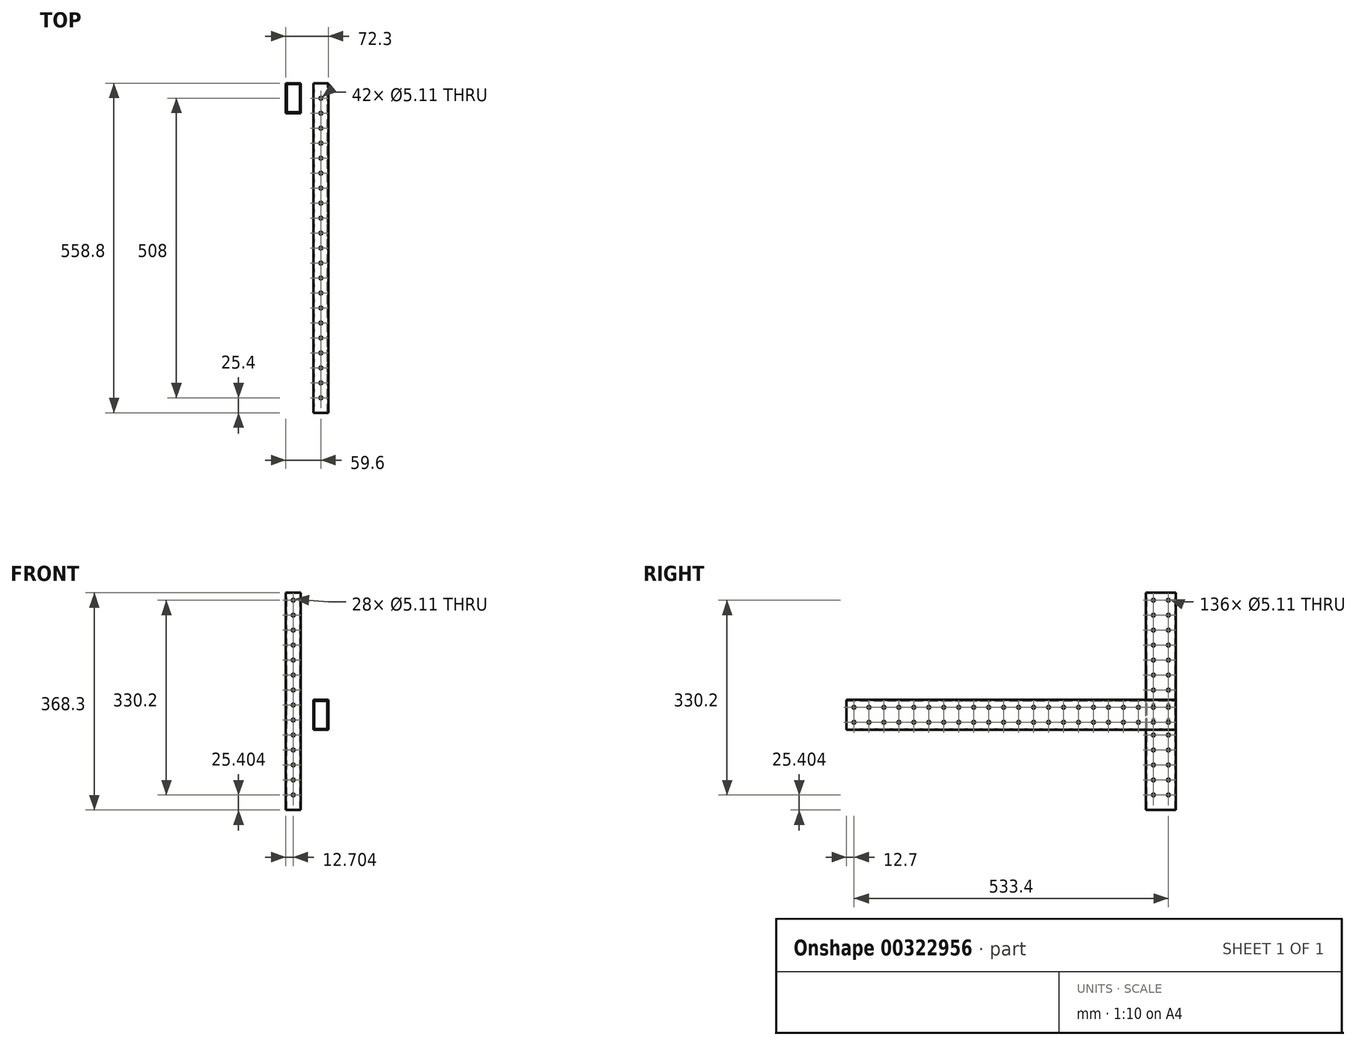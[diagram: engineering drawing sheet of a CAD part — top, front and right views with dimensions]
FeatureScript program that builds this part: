
annotation { "Feature Type Name" : "Feature", "Feature Type Description" : "" }
export const myFeature = defineFeature(function(context is Context, id is Id, definition is map)
    precondition{}
    {
        {
            var Q0;
            Q0=qCreatedBy(makeId("Front.planeOp"),FACE);
            var sketch = newSketch(context, id + "F0", { "sketchPlane" : qUnion([Q0])});
            skLineSegment(sketch, "E0.bottom", {"start": v(-59.6, -161.33) * mm, "end": v(-34.2, -161.33) * mm});
            skLineSegment(sketch, "E0.top", {"start": v(-59.6, 206.97) * mm, "end": v(-34.2, 206.97) * mm});
            skLineSegment(sketch, "E0.left", {"start": v(-59.6, -161.33) * mm, "end": v(-59.6, 206.97) * mm});
            skLineSegment(sketch, "E0.right", {"start": v(-34.2, -161.33) * mm, "end": v(-34.2, 206.97) * mm});
            skSolve(sketch);
        }
        {
            var Q0;
            Q0=makeQuery(id+"F0.imprint","IMPRINT",FACE,{"disambiguationData":[TD([[makeQuery(id+"F0.imprint","IMPRINT",EDGE,{"derivedFrom":sQuery(id+"F0.wireOp",EDGE,"E0.bottom")}),1.0]])]});
            extrude(context, id + "F1", {"entities" : qUnion([Q0]), "depth" : 50.8 * mm});
        }
        {
            var Q0;
            Q0=qCreatedBy(makeId("Front.planeOp"),FACE);
            var sketch = newSketch(context, id + "F2", { "sketchPlane" : qUnion([Q0])});
            skLineSegment(sketch, "E1.bottom", {"start": v(12.7, -25.4) * mm, "end": v(-12.7, -25.4) * mm});
            skLineSegment(sketch, "E1.top", {"start": v(12.7, 25.4) * mm, "end": v(-12.7, 25.4) * mm});
            skLineSegment(sketch, "E1.left", {"start": v(12.7, -25.4) * mm, "end": v(12.7, 25.4) * mm});
            skLineSegment(sketch, "E1.right", {"start": v(-12.7, -25.4) * mm, "end": v(-12.7, 25.4) * mm});
            skPoint(sketch, "E1.middle", {"position": v(0, 0) * mm});
            skLineSegment(sketch, "E2.bottom", {"start": v(11.11, -23.81) * mm, "end": v(-11.11, -23.81) * mm});
            skLineSegment(sketch, "E2.top", {"start": v(11.11, 23.81) * mm, "end": v(-11.11, 23.81) * mm});
            skLineSegment(sketch, "E2.left", {"start": v(11.11, -23.81) * mm, "end": v(11.11, 23.81) * mm});
            skLineSegment(sketch, "E2.right", {"start": v(-11.11, -23.81) * mm, "end": v(-11.11, 23.81) * mm});
            skSolve(sketch);
        }
        {
            var Q0;
            Q0=makeQuery(id+"F2.imprint","IMPRINT",FACE,{"disambiguationData":[TD([[makeQuery(id+"F2.imprint","IMPRINT",EDGE,{"derivedFrom":sQuery(id+"F2.wireOp",EDGE,"E1.bottom")}),-1.0]])]});
            extrude(context, id + "F3", {"entities" : qUnion([Q0]), "depth" : 558.8 * mm});
        }
        {
            var Q0;
            Q0=makeQuery(id+"F3.opExtrude","SWEPT_FACE",FACE,{"disambiguationData":[OSD([sQuery(id+"F2.wireOp",EDGE,"E1.top")])]});
            var sketch = newSketch(context, id + "F4", { "sketchPlane" : qUnion([Q0])});
            skCircle(sketch, "E3", {"center": v(0, -533.4) * mm, "radius": 2.55 * mm});
            skCircle(sketch, "E4.1.0.0", {"center": v(0, -508) * mm, "radius": 2.55 * mm});
            skCircle(sketch, "E4.2.0.0", {"center": v(0, -482.6) * mm, "radius": 2.55 * mm});
            skCircle(sketch, "E4.3.0.0", {"center": v(0, -457.2) * mm, "radius": 2.55 * mm});
            skCircle(sketch, "E4.4.0.0", {"center": v(0, -431.8) * mm, "radius": 2.55 * mm});
            skCircle(sketch, "E4.5.0.0", {"center": v(0, -406.4) * mm, "radius": 2.55 * mm});
            skCircle(sketch, "E4.6.0.0", {"center": v(0, -381) * mm, "radius": 2.55 * mm});
            skCircle(sketch, "E4.7.0.0", {"center": v(0, -355.6) * mm, "radius": 2.55 * mm});
            skCircle(sketch, "E4.8.0.0", {"center": v(0, -330.2) * mm, "radius": 2.55 * mm});
            skCircle(sketch, "E4.9.0.0", {"center": v(0, -304.8) * mm, "radius": 2.55 * mm});
            skCircle(sketch, "E4.10.0.0", {"center": v(0, -279.4) * mm, "radius": 2.55 * mm});
            skCircle(sketch, "E4.11.0.0", {"center": v(0, -254) * mm, "radius": 2.55 * mm});
            skCircle(sketch, "E4.12.0.0", {"center": v(0, -228.6) * mm, "radius": 2.55 * mm});
            skCircle(sketch, "E4.13.0.0", {"center": v(0, -203.2) * mm, "radius": 2.55 * mm});
            skCircle(sketch, "E4.14.0.0", {"center": v(0, -177.8) * mm, "radius": 2.55 * mm});
            skCircle(sketch, "E4.15.0.0", {"center": v(0, -152.4) * mm, "radius": 2.55 * mm});
            skCircle(sketch, "E4.16.0.0", {"center": v(0, -127) * mm, "radius": 2.55 * mm});
            skCircle(sketch, "E4.17.0.0", {"center": v(0, -101.6) * mm, "radius": 2.55 * mm});
            skCircle(sketch, "E4.18.0.0", {"center": v(0, -76.2) * mm, "radius": 2.55 * mm});
            skCircle(sketch, "E4.19.0.0", {"center": v(0, -50.8) * mm, "radius": 2.55 * mm});
            skCircle(sketch, "E4.20.0.0", {"center": v(0, -25.4) * mm, "radius": 2.55 * mm});
            skLineSegment(sketch, "E4.direction1", {"start": v(0, -533.4) * mm, "end": v(0, -508) * mm, "construction": true});
            skSolve(sketch);
        }
        {
            var Q0;
            Q0=makeQuery(id+"F1.opExtrude","CAP_FACE",FACE,{"disambiguationData":[OSD([sQuery(id+"F0.wireOp",EDGE,"E0.bottom"),sQuery(id+"F0.wireOp",EDGE,"E0.top"),sQuery(id+"F0.wireOp",EDGE,"E0.left"),sQuery(id+"F0.wireOp",EDGE,"E0.right")])],"isStart":false});
            var sketch = newSketch(context, id + "F5", { "sketchPlane" : qUnion([Q0])});
            skCircle(sketch, "E5", {"center": v(-46.9, 194.27) * mm, "radius": 2.55 * mm});
            skCircle(sketch, "E6.0.1.0", {"center": v(-46.9, 168.87) * mm, "radius": 2.55 * mm});
            skCircle(sketch, "E6.0.2.0", {"center": v(-46.9, 143.47) * mm, "radius": 2.55 * mm});
            skCircle(sketch, "E6.0.3.0", {"center": v(-46.9, 118.07) * mm, "radius": 2.55 * mm});
            skCircle(sketch, "E6.0.4.0", {"center": v(-46.9, 92.67) * mm, "radius": 2.55 * mm});
            skCircle(sketch, "E6.0.5.0", {"center": v(-46.9, 67.27) * mm, "radius": 2.55 * mm});
            skCircle(sketch, "E6.0.6.0", {"center": v(-46.9, 41.87) * mm, "radius": 2.55 * mm});
            skCircle(sketch, "E6.0.7.0", {"center": v(-46.9, 16.47) * mm, "radius": 2.55 * mm});
            skCircle(sketch, "E6.0.8.0", {"center": v(-46.9, -8.93) * mm, "radius": 2.55 * mm});
            skCircle(sketch, "E6.0.9.0", {"center": v(-46.9, -34.33) * mm, "radius": 2.55 * mm});
            skCircle(sketch, "E6.0.10.0", {"center": v(-46.9, -59.73) * mm, "radius": 2.55 * mm});
            skCircle(sketch, "E6.0.11.0", {"center": v(-46.9, -85.13) * mm, "radius": 2.55 * mm});
            skCircle(sketch, "E6.0.12.0", {"center": v(-46.9, -110.53) * mm, "radius": 2.55 * mm});
            skCircle(sketch, "E6.0.13.0", {"center": v(-46.9, -135.93) * mm, "radius": 2.55 * mm});
            skLineSegment(sketch, "E6.direction1", {"start": v(-46.9, 194.27) * mm, "end": v(-21.5, 194.27) * mm, "construction": true});
            skLineSegment(sketch, "E6.direction2", {"start": v(-46.9, 194.27) * mm, "end": v(-46.9, 168.87) * mm, "construction": true});
            skSolve(sketch);
        }
        {
            var Q0;
            Q0=sQuery(id+"F4.wireOp",VERTEX,"E3.center");
            var Q1;
            Q1=sQuery(id+"F4.wireOp",VERTEX,"E4.1.0.0.center");
            var Q2;
            Q2=sQuery(id+"F4.wireOp",VERTEX,"E4.2.0.0.center");
            var Q3;
            Q3=sQuery(id+"F4.wireOp",VERTEX,"E4.3.0.0.center");
            var Q4;
            Q4=sQuery(id+"F4.wireOp",VERTEX,"E4.4.0.0.center");
            var Q5;
            Q5=sQuery(id+"F4.wireOp",VERTEX,"E4.5.0.0.center");
            var Q6;
            Q6=sQuery(id+"F4.wireOp",VERTEX,"E4.6.0.0.center");
            var Q7;
            Q7=sQuery(id+"F4.wireOp",VERTEX,"E4.7.0.0.center");
            var Q8;
            Q8=sQuery(id+"F4.wireOp",VERTEX,"E4.11.0.0.center");
            var Q9;
            Q9=sQuery(id+"F4.wireOp",VERTEX,"E4.9.0.0.center");
            var Q10;
            Q10=sQuery(id+"F4.wireOp",VERTEX,"E4.10.0.0.center");
            var Q11;
            Q11=sQuery(id+"F4.wireOp",VERTEX,"E4.12.0.0.center");
            var Q12;
            Q12=sQuery(id+"F4.wireOp",VERTEX,"E4.13.0.0.center");
            var Q13;
            Q13=sQuery(id+"F4.wireOp",VERTEX,"E4.14.0.0.center");
            var Q14;
            Q14=sQuery(id+"F4.wireOp",VERTEX,"E4.15.0.0.center");
            var Q15;
            Q15=sQuery(id+"F4.wireOp",VERTEX,"E4.17.0.0.center");
            var Q16;
            Q16=sQuery(id+"F4.wireOp",VERTEX,"E4.16.0.0.center");
            var Q17;
            Q17=sQuery(id+"F4.wireOp",VERTEX,"E4.19.0.0.center");
            var Q18;
            Q18=sQuery(id+"F4.wireOp",VERTEX,"E4.18.0.0.center");
            var Q19;
            Q19=sQuery(id+"F4.wireOp",VERTEX,"E4.20.0.0.center");
            var Q20;
            Q20=sQuery(id+"F4.wireOp",VERTEX,"E4.8.0.0.center");
            var Q21;
            Q21=makeQuery(id+"F3.opExtrude","SWEPT_BODY",BODY,{"disambiguationData":[OSD([sQuery(id+"F2.wireOp",EDGE,"E1.bottom"),sQuery(id+"F2.wireOp",EDGE,"E1.top"),sQuery(id+"F2.wireOp",EDGE,"E1.left"),sQuery(id+"F2.wireOp",EDGE,"E1.right"),sQuery(id+"F2.wireOp",EDGE,"E2.bottom"),sQuery(id+"F2.wireOp",EDGE,"E2.top"),sQuery(id+"F2.wireOp",EDGE,"E2.left"),sQuery(id+"F2.wireOp",EDGE,"E2.right")])]});
            hole(context, id + "F6", {"style" : HoleStyle.SIMPLE, "endStyle" : HoleEndStyle.THROUGH, "holeDiameter" : 5.1 * mm, "isTappedThrough" : true, "tappedDepth" : 12.7 * mm, "tapClearance" : 3, "locations" : qUnion([Q0, Q1, Q2, Q3, Q4, Q5, Q6, Q7, Q8, Q9, Q10, Q11, Q12, Q13, Q14, Q15, Q16, Q17, Q18, Q19, Q20]), "scope" : qUnion([Q21])});
        }
        {
            var Q0;
            Q0 = qSketchRegion(id + "F5", true);
            extrude(context, id + "F7", {"entities" : qUnion([Q0]), "operationType" : NewBodyOperationType.REMOVE, "oppositeDirection" : true, "depth" : 50.8 * mm});
        }
        {
            var Q0;
            Q0=makeQuery(id+"F1.opExtrude","SWEPT_FACE",FACE,{"disambiguationData":[OSD([sQuery(id+"F0.wireOp",EDGE,"E0.top")])]});
            var sketch = newSketch(context, id + "F8", { "sketchPlane" : qUnion([Q0])});
            skLineSegment(sketch, "E7.bottom", {"start": v(-58, -1.59) * mm, "end": v(-35.8, -1.59) * mm});
            skLineSegment(sketch, "E7.top", {"start": v(-58, -49.2) * mm, "end": v(-35.8, -49.2) * mm});
            skLineSegment(sketch, "E7.left", {"start": v(-58, -1.59) * mm, "end": v(-58, -49.2) * mm});
            skLineSegment(sketch, "E7.right", {"start": v(-35.8, -1.59) * mm, "end": v(-35.8, -49.2) * mm});
            skSolve(sketch);
        }
        {
            var Q0;
            Q0=makeQuery(id+"F8.imprint","IMPRINT",FACE,{"disambiguationData":[TD([[makeQuery(id+"F8.imprint","IMPRINT",EDGE,{"derivedFrom":sQuery(id+"F8.wireOp",EDGE,"E7.bottom")}),-1.0]])]});
            extrude(context, id + "F9", {"entities" : qUnion([Q0]), "operationType" : NewBodyOperationType.REMOVE, "oppositeDirection" : true, "depth" : 381 * mm});
        }
        {
            var Q0;
            Q0=makeQuery(id+"F1.opExtrude","SWEPT_FACE",FACE,{"disambiguationData":[OSD([sQuery(id+"F0.wireOp",EDGE,"E0.left")])]});
            var sketch = newSketch(context, id + "F10", { "sketchPlane" : qUnion([Q0])});
            skCircle(sketch, "E8", {"center": v(12.7, 194.27) * mm, "radius": 2.55 * mm});
            skCircle(sketch, "E9.0.1.0", {"center": v(12.7, 168.87) * mm, "radius": 2.55 * mm});
            skCircle(sketch, "E9.0.2.0", {"center": v(12.7, 143.47) * mm, "radius": 2.55 * mm});
            skCircle(sketch, "E9.0.3.0", {"center": v(12.7, 118.07) * mm, "radius": 2.55 * mm});
            skCircle(sketch, "E9.0.4.0", {"center": v(12.7, 92.67) * mm, "radius": 2.55 * mm});
            skCircle(sketch, "E9.0.5.0", {"center": v(12.7, 67.27) * mm, "radius": 2.55 * mm});
            skCircle(sketch, "E9.0.6.0", {"center": v(12.7, 41.87) * mm, "radius": 2.55 * mm});
            skCircle(sketch, "E9.0.7.0", {"center": v(12.7, 16.47) * mm, "radius": 2.55 * mm});
            skCircle(sketch, "E9.0.8.0", {"center": v(12.7, -8.93) * mm, "radius": 2.55 * mm});
            skCircle(sketch, "E9.0.9.0", {"center": v(12.7, -34.33) * mm, "radius": 2.55 * mm});
            skCircle(sketch, "E9.0.10.0", {"center": v(12.7, -59.73) * mm, "radius": 2.55 * mm});
            skCircle(sketch, "E9.0.11.0", {"center": v(12.7, -85.13) * mm, "radius": 2.55 * mm});
            skCircle(sketch, "E9.0.12.0", {"center": v(12.7, -110.53) * mm, "radius": 2.55 * mm});
            skCircle(sketch, "E9.0.13.0", {"center": v(12.7, -135.93) * mm, "radius": 2.55 * mm});
            skCircle(sketch, "E9.1.0.0", {"center": v(38.1, 194.27) * mm, "radius": 2.55 * mm});
            skCircle(sketch, "E9.1.1.0", {"center": v(38.1, 168.87) * mm, "radius": 2.55 * mm});
            skCircle(sketch, "E9.1.2.0", {"center": v(38.1, 143.47) * mm, "radius": 2.55 * mm});
            skCircle(sketch, "E9.1.3.0", {"center": v(38.1, 118.07) * mm, "radius": 2.55 * mm});
            skCircle(sketch, "E9.1.4.0", {"center": v(38.1, 92.67) * mm, "radius": 2.55 * mm});
            skCircle(sketch, "E9.1.5.0", {"center": v(38.1, 67.27) * mm, "radius": 2.55 * mm});
            skCircle(sketch, "E9.1.6.0", {"center": v(38.1, 41.87) * mm, "radius": 2.55 * mm});
            skCircle(sketch, "E9.1.7.0", {"center": v(38.1, 16.47) * mm, "radius": 2.55 * mm});
            skCircle(sketch, "E9.1.8.0", {"center": v(38.1, -8.93) * mm, "radius": 2.55 * mm});
            skCircle(sketch, "E9.1.9.0", {"center": v(38.1, -34.33) * mm, "radius": 2.55 * mm});
            skCircle(sketch, "E9.1.10.0", {"center": v(38.1, -59.73) * mm, "radius": 2.55 * mm});
            skCircle(sketch, "E9.1.11.0", {"center": v(38.1, -85.13) * mm, "radius": 2.55 * mm});
            skCircle(sketch, "E9.1.12.0", {"center": v(38.1, -110.53) * mm, "radius": 2.55 * mm});
            skCircle(sketch, "E9.1.13.0", {"center": v(38.1, -135.93) * mm, "radius": 2.55 * mm});
            skLineSegment(sketch, "E9.direction1", {"start": v(12.7, 194.27) * mm, "end": v(38.1, 194.27) * mm, "construction": true});
            skLineSegment(sketch, "E9.direction2", {"start": v(12.7, 194.27) * mm, "end": v(12.7, 168.87) * mm, "construction": true});
            skSolve(sketch);
        }
        {
            var Q0;
            Q0 = qSketchRegion(id + "F10", true);
            extrude(context, id + "F11", {"entities" : qUnion([Q0]), "operationType" : NewBodyOperationType.REMOVE, "oppositeDirection" : true, "depth" : 25.4 * mm});
        }
        {
            var Q0;
            Q0=makeQuery(id+"F3.opExtrude","SWEPT_FACE",FACE,{"disambiguationData":[OSD([sQuery(id+"F2.wireOp",EDGE,"E1.left")])]});
            var sketch = newSketch(context, id + "F12", { "sketchPlane" : qUnion([Q0])});
            skCircle(sketch, "E10", {"center": v(-546.1, 12.7) * mm, "radius": 2.55 * mm});
            skCircle(sketch, "E11", {"center": v(-546.1, -12.7) * mm, "radius": 2.55 * mm});
            skCircle(sketch, "E12.1.0.0", {"center": v(-520.7, 12.7) * mm, "radius": 2.55 * mm});
            skCircle(sketch, "E12.1.0.1", {"center": v(-520.7, -12.7) * mm, "radius": 2.55 * mm});
            skCircle(sketch, "E12.2.0.0", {"center": v(-495.3, 12.7) * mm, "radius": 2.55 * mm});
            skCircle(sketch, "E12.2.0.1", {"center": v(-495.3, -12.7) * mm, "radius": 2.55 * mm});
            skCircle(sketch, "E12.3.0.0", {"center": v(-469.9, 12.7) * mm, "radius": 2.55 * mm});
            skCircle(sketch, "E12.3.0.1", {"center": v(-469.9, -12.7) * mm, "radius": 2.55 * mm});
            skCircle(sketch, "E12.4.0.0", {"center": v(-444.5, 12.7) * mm, "radius": 2.55 * mm});
            skCircle(sketch, "E12.4.0.1", {"center": v(-444.5, -12.7) * mm, "radius": 2.55 * mm});
            skCircle(sketch, "E12.5.0.0", {"center": v(-419.1, 12.7) * mm, "radius": 2.55 * mm});
            skCircle(sketch, "E12.5.0.1", {"center": v(-419.1, -12.7) * mm, "radius": 2.55 * mm});
            skCircle(sketch, "E12.6.0.0", {"center": v(-393.7, 12.7) * mm, "radius": 2.55 * mm});
            skCircle(sketch, "E12.6.0.1", {"center": v(-393.7, -12.7) * mm, "radius": 2.55 * mm});
            skCircle(sketch, "E12.7.0.0", {"center": v(-368.3, 12.7) * mm, "radius": 2.55 * mm});
            skCircle(sketch, "E12.7.0.1", {"center": v(-368.3, -12.7) * mm, "radius": 2.55 * mm});
            skCircle(sketch, "E12.8.0.0", {"center": v(-342.9, 12.7) * mm, "radius": 2.55 * mm});
            skCircle(sketch, "E12.8.0.1", {"center": v(-342.9, -12.7) * mm, "radius": 2.55 * mm});
            skCircle(sketch, "E12.9.0.0", {"center": v(-317.5, 12.7) * mm, "radius": 2.55 * mm});
            skCircle(sketch, "E12.9.0.1", {"center": v(-317.5, -12.7) * mm, "radius": 2.55 * mm});
            skCircle(sketch, "E12.10.0.0", {"center": v(-292.1, 12.7) * mm, "radius": 2.55 * mm});
            skCircle(sketch, "E12.10.0.1", {"center": v(-292.1, -12.7) * mm, "radius": 2.55 * mm});
            skCircle(sketch, "E12.11.0.0", {"center": v(-266.7, 12.7) * mm, "radius": 2.55 * mm});
            skCircle(sketch, "E12.11.0.1", {"center": v(-266.7, -12.7) * mm, "radius": 2.55 * mm});
            skCircle(sketch, "E12.12.0.0", {"center": v(-241.3, 12.7) * mm, "radius": 2.55 * mm});
            skCircle(sketch, "E12.12.0.1", {"center": v(-241.3, -12.7) * mm, "radius": 2.55 * mm});
            skCircle(sketch, "E12.13.0.0", {"center": v(-215.9, 12.7) * mm, "radius": 2.55 * mm});
            skCircle(sketch, "E12.13.0.1", {"center": v(-215.9, -12.7) * mm, "radius": 2.55 * mm});
            skCircle(sketch, "E12.14.0.0", {"center": v(-190.5, 12.7) * mm, "radius": 2.55 * mm});
            skCircle(sketch, "E12.14.0.1", {"center": v(-190.5, -12.7) * mm, "radius": 2.55 * mm});
            skCircle(sketch, "E12.15.0.0", {"center": v(-165.1, 12.7) * mm, "radius": 2.55 * mm});
            skCircle(sketch, "E12.15.0.1", {"center": v(-165.1, -12.7) * mm, "radius": 2.55 * mm});
            skCircle(sketch, "E12.16.0.0", {"center": v(-139.7, 12.7) * mm, "radius": 2.55 * mm});
            skCircle(sketch, "E12.16.0.1", {"center": v(-139.7, -12.7) * mm, "radius": 2.55 * mm});
            skCircle(sketch, "E12.17.0.0", {"center": v(-114.3, 12.7) * mm, "radius": 2.55 * mm});
            skCircle(sketch, "E12.17.0.1", {"center": v(-114.3, -12.7) * mm, "radius": 2.55 * mm});
            skCircle(sketch, "E12.18.0.0", {"center": v(-88.9, 12.7) * mm, "radius": 2.55 * mm});
            skCircle(sketch, "E12.18.0.1", {"center": v(-88.9, -12.7) * mm, "radius": 2.55 * mm});
            skCircle(sketch, "E12.19.0.0", {"center": v(-63.5, 12.7) * mm, "radius": 2.55 * mm});
            skCircle(sketch, "E12.19.0.1", {"center": v(-63.5, -12.7) * mm, "radius": 2.55 * mm});
            skCircle(sketch, "E12.20.0.0", {"center": v(-38.1, 12.7) * mm, "radius": 2.55 * mm});
            skCircle(sketch, "E12.20.0.1", {"center": v(-38.1, -12.7) * mm, "radius": 2.55 * mm});
            skCircle(sketch, "E12.21.0.0", {"center": v(-12.7, 12.7) * mm, "radius": 2.55 * mm});
            skCircle(sketch, "E12.21.0.1", {"center": v(-12.7, -12.7) * mm, "radius": 2.55 * mm});
            skLineSegment(sketch, "E12.direction1", {"start": v(-546.1, 12.7) * mm, "end": v(-520.7, 12.7) * mm, "construction": true});
            skSolve(sketch);
        }
        {
            var Q0;
            Q0=sQuery(id+"F12.wireOp",VERTEX,"E12.3.0.0.center");
            var Q1;
            Q1=sQuery(id+"F12.wireOp",VERTEX,"E12.5.0.1.center");
            var Q2;
            Q2=sQuery(id+"F12.wireOp",VERTEX,"E12.2.0.0.center");
            var Q3;
            Q3=sQuery(id+"F12.wireOp",VERTEX,"E12.1.0.1.center");
            var Q4;
            Q4=sQuery(id+"F12.wireOp",VERTEX,"E12.20.0.0.center");
            var Q5;
            Q5=sQuery(id+"F12.wireOp",VERTEX,"E12.12.0.0.center");
            var Q6;
            Q6=sQuery(id+"F12.wireOp",VERTEX,"E12.2.0.1.center");
            var Q7;
            Q7=sQuery(id+"F12.wireOp",VERTEX,"E12.4.0.0.center");
            var Q8;
            Q8=sQuery(id+"F12.wireOp",VERTEX,"E12.3.0.1.center");
            var Q9;
            Q9=sQuery(id+"F12.wireOp",VERTEX,"E12.6.0.1.center");
            var Q10;
            Q10=sQuery(id+"F12.wireOp",VERTEX,"E12.6.0.0.center");
            var Q11;
            Q11=sQuery(id+"F12.wireOp",VERTEX,"E10.center");
            var Q12;
            Q12=sQuery(id+"F12.wireOp",VERTEX,"E12.16.0.1.center");
            var Q13;
            Q13=sQuery(id+"F12.wireOp",VERTEX,"E12.8.0.1.center");
            var Q14;
            Q14=sQuery(id+"F12.wireOp",VERTEX,"E12.1.0.0.center");
            var Q15;
            Q15=sQuery(id+"F12.wireOp",VERTEX,"E11.center");
            var Q16;
            Q16=sQuery(id+"F12.wireOp",VERTEX,"E12.14.0.1.center");
            var Q17;
            Q17=sQuery(id+"F12.wireOp",VERTEX,"E12.18.0.0.center");
            var Q18;
            Q18=sQuery(id+"F12.wireOp",VERTEX,"E12.10.0.0.center");
            var Q19;
            Q19=sQuery(id+"F12.wireOp",VERTEX,"E12.5.0.0.center");
            var Q20;
            Q20=sQuery(id+"F12.wireOp",VERTEX,"E12.4.0.1.center");
            var Q21;
            Q21=sQuery(id+"F12.wireOp",VERTEX,"E12.19.0.1.center");
            var Q22;
            Q22=sQuery(id+"F12.wireOp",VERTEX,"E12.11.0.1.center");
            var Q23;
            Q23=sQuery(id+"F12.wireOp",VERTEX,"E12.16.0.0.center");
            var Q24;
            Q24=sQuery(id+"F12.wireOp",VERTEX,"E12.8.0.0.center");
            var Q25;
            Q25=sQuery(id+"F12.wireOp",VERTEX,"E12.19.0.0.center");
            var Q26;
            Q26=sQuery(id+"F12.wireOp",VERTEX,"E12.11.0.0.center");
            var Q27;
            Q27=sQuery(id+"F12.wireOp",VERTEX,"E12.15.0.1.center");
            var Q28;
            Q28=sQuery(id+"F12.wireOp",VERTEX,"E12.7.0.1.center");
            var Q29;
            Q29=sQuery(id+"F12.wireOp",VERTEX,"E12.21.0.0.center");
            var Q30;
            Q30=sQuery(id+"F12.wireOp",VERTEX,"E12.13.0.0.center");
            var Q31;
            Q31=sQuery(id+"F12.wireOp",VERTEX,"E12.17.0.1.center");
            var Q32;
            Q32=sQuery(id+"F12.wireOp",VERTEX,"E12.14.0.0.center");
            var Q33;
            Q33=sQuery(id+"F12.wireOp",VERTEX,"E12.9.0.1.center");
            var Q34;
            Q34=sQuery(id+"F12.wireOp",VERTEX,"E12.18.0.1.center");
            var Q35;
            Q35=sQuery(id+"F12.wireOp",VERTEX,"E12.10.0.1.center");
            var Q36;
            Q36=sQuery(id+"F12.wireOp",VERTEX,"E12.20.0.1.center");
            var Q37;
            Q37=sQuery(id+"F12.wireOp",VERTEX,"E12.12.0.1.center");
            var Q38;
            Q38=sQuery(id+"F12.wireOp",VERTEX,"E12.15.0.0.center");
            var Q39;
            Q39=sQuery(id+"F12.wireOp",VERTEX,"E12.7.0.0.center");
            var Q40;
            Q40=sQuery(id+"F12.wireOp",VERTEX,"E12.13.0.1.center");
            var Q41;
            Q41=sQuery(id+"F12.wireOp",VERTEX,"E12.17.0.0.center");
            var Q42;
            Q42=sQuery(id+"F12.wireOp",VERTEX,"E12.9.0.0.center");
            var Q43;
            Q43=sQuery(id+"F12.wireOp",VERTEX,"E12.21.0.1.center");
            var Q44;
            Q44=makeQuery(id+"F3.opExtrude","SWEPT_BODY",BODY,{"disambiguationData":[OSD([sQuery(id+"F2.wireOp",EDGE,"E1.bottom"),sQuery(id+"F2.wireOp",EDGE,"E1.top"),sQuery(id+"F2.wireOp",EDGE,"E1.left"),sQuery(id+"F2.wireOp",EDGE,"E1.right"),sQuery(id+"F2.wireOp",EDGE,"E2.bottom"),sQuery(id+"F2.wireOp",EDGE,"E2.top"),sQuery(id+"F2.wireOp",EDGE,"E2.left"),sQuery(id+"F2.wireOp",EDGE,"E2.right")])]});
            var Q45;
            Q45=makeQuery(id+"F1.opExtrude","SWEPT_BODY",BODY,{"disambiguationData":[OSD([sQuery(id+"F0.wireOp",EDGE,"E0.bottom"),sQuery(id+"F0.wireOp",EDGE,"E0.top"),sQuery(id+"F0.wireOp",EDGE,"E0.left"),sQuery(id+"F0.wireOp",EDGE,"E0.right")])]});
            hole(context, id + "F13", {"style" : HoleStyle.SIMPLE, "endStyle" : HoleEndStyle.THROUGH, "holeDiameter" : 5.1 * mm, "isTappedThrough" : true, "tappedDepth" : 12.7 * mm, "tapClearance" : 3, "locations" : qUnion([Q0, Q1, Q2, Q3, Q4, Q5, Q6, Q7, Q8, Q9, Q10, Q11, Q12, Q13, Q14, Q15, Q16, Q17, Q18, Q19, Q20, Q21, Q22, Q23, Q24, Q25, Q26, Q27, Q28, Q29, Q30, Q31, Q32, Q33, Q34, Q35, Q36, Q37, Q38, Q39, Q40, Q41, Q42, Q43]), "scope" : qUnion([Q44, Q45])});
        }
    });
